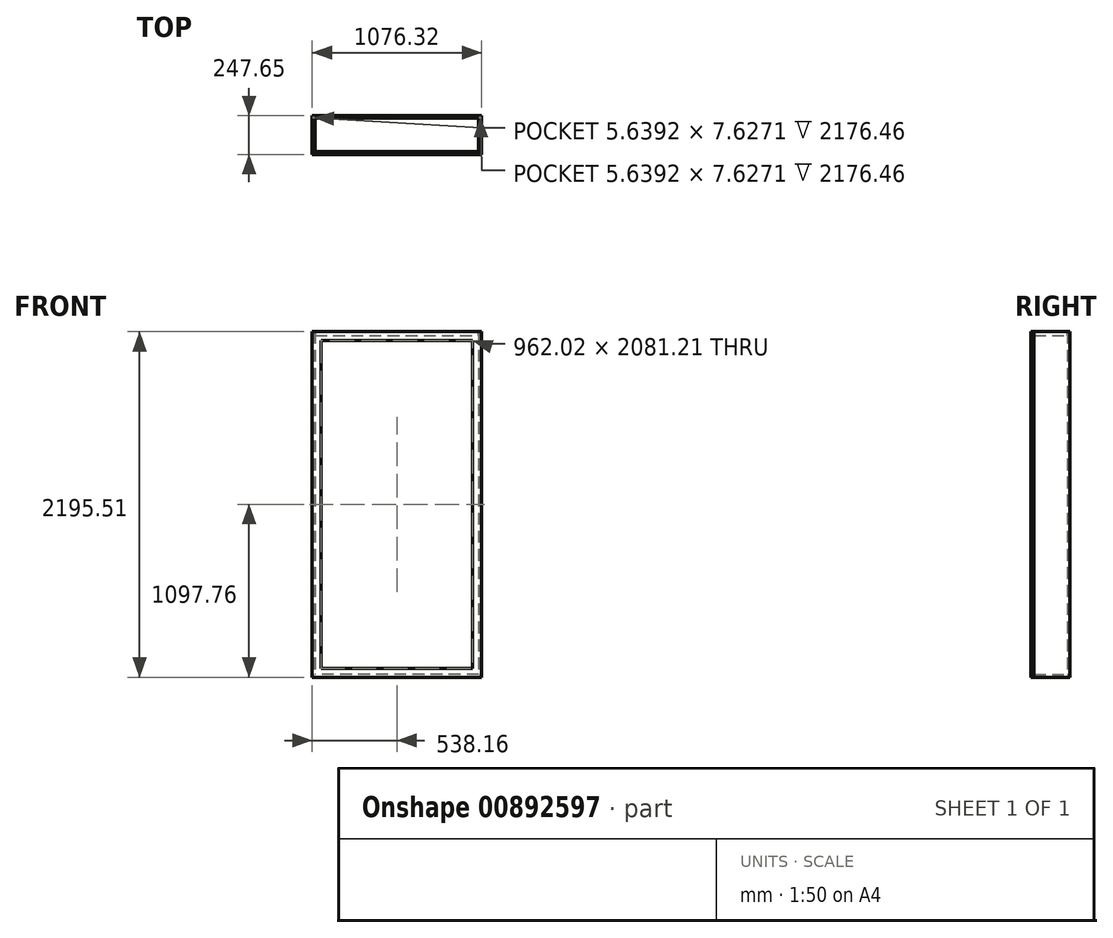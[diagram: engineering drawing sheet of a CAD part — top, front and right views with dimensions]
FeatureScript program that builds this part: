
annotation { "Feature Type Name" : "Feature", "Feature Type Description" : "" }
export const myFeature = defineFeature(function(context is Context, id is Id, definition is map)
    precondition{}
    {
        {
            var Q0;
            Q0=qCreatedBy(makeId("Top.planeOp"),FACE);
            var sketch = newSketch(context, id + "F0", { "sketchPlane" : qUnion([Q0])});
            skLineSegment(sketch, "E0.bottom", {"start": v(538.16, 228.6) * mm, "end": v(-538.16, 228.6) * mm});
            skLineSegment(sketch, "E0.top", {"start": v(538.16, 0) * mm, "end": v(-538.16, 0) * mm});
            skLineSegment(sketch, "E0.left", {"start": v(538.16, 228.6) * mm, "end": v(538.16, 0) * mm});
            skLineSegment(sketch, "E0.right", {"start": v(-538.16, 228.6) * mm, "end": v(-538.16, 0) * mm});
            skSolve(sketch);
        }
        {
            var Q0;
            Q0=makeQuery(id+"F0.imprint","IMPRINT",FACE,{"disambiguationData":[TD([[makeQuery(id+"F0.imprint","IMPRINT",EDGE,{"derivedFrom":sQuery(id+"F0.wireOp",EDGE,"E0.bottom")}),1.0]])]});
            extrude(context, id + "F1", {"entities" : qUnion([Q0]), "depth" : 19.05 * mm, "offsetDistance" : 25.4 * mm});
        }
        {
            var Q0;
            Q0=makeQuery(id+"F1.opExtrude","CAP_FACE",FACE,{"disambiguationData":[OSD([sQuery(id+"F0.wireOp",EDGE,"E0.bottom"),sQuery(id+"F0.wireOp",EDGE,"E0.top"),sQuery(id+"F0.wireOp",EDGE,"E0.left"),sQuery(id+"F0.wireOp",EDGE,"E0.right")])],"isStart":false});
            var sketch = newSketch(context, id + "F2", { "sketchPlane" : qUnion([Q0])});
            skLineSegment(sketch, "E1.bottom", {"start": v(-538.16, 228.6) * mm, "end": v(-519.11, 228.6) * mm});
            skLineSegment(sketch, "E1.top", {"start": v(-538.16, 0) * mm, "end": v(-519.11, 0) * mm});
            skLineSegment(sketch, "E1.left", {"start": v(-538.16, 228.6) * mm, "end": v(-538.16, 0) * mm});
            skLineSegment(sketch, "E1.right", {"start": v(-519.11, 228.6) * mm, "end": v(-519.11, 0) * mm});
            skLineSegment(sketch, "E2.bottom", {"start": v(538.16, 228.6) * mm, "end": v(519.11, 228.6) * mm});
            skLineSegment(sketch, "E2.top", {"start": v(538.16, 0) * mm, "end": v(519.11, 0) * mm});
            skLineSegment(sketch, "E2.left", {"start": v(538.16, 228.6) * mm, "end": v(538.16, 0) * mm});
            skLineSegment(sketch, "E2.right", {"start": v(519.11, 228.6) * mm, "end": v(519.11, 0) * mm});
            skSolve(sketch);
        }
        {
            var Q0;
            Q0=makeQuery(id+"F1.opExtrude","CAP_FACE",FACE,{"disambiguationData":[OSD([sQuery(id+"F0.wireOp",EDGE,"E0.bottom"),sQuery(id+"F0.wireOp",EDGE,"E0.top"),sQuery(id+"F0.wireOp",EDGE,"E0.left"),sQuery(id+"F0.wireOp",EDGE,"E0.right")])],"isStart":false});
            var sketch = newSketch(context, id + "F3", { "sketchPlane" : qUnion([Q0])});
            skLineSegment(sketch, "E3.bottom", {"start": v(-538.16, 0) * mm, "end": v(-519.11, 0) * mm});
            skLineSegment(sketch, "E3.left", {"start": v(-538.16, 0) * mm, "end": v(-538.16, 209.55) * mm});
            skLineSegment(sketch, "E3.right", {"start": v(-519.11, 0) * mm, "end": v(-519.11, 209.55) * mm});
            skLineSegment(sketch, "E4", {"start": v(-528.64, 220.5) * mm, "end": v(-531.46, 220.5) * mm});
            skLineSegment(sketch, "E5", {"start": v(-538.16, 209.55) * mm, "end": v(-538.16, 212.88) * mm});
            skLineSegment(sketch, "E6", {"start": v(-538.16, 212.88) * mm, "end": v(-531.46, 212.88) * mm});
            skLineSegment(sketch, "E7", {"start": v(-531.46, 212.88) * mm, "end": v(-531.46, 220.5) * mm});
            skLineSegment(sketch, "E8.MirrorCS", {"start": v(-528.64, 220.5) * mm, "end": v(-525.82, 220.5) * mm});
            skLineSegment(sketch, "E9.MirrorCS", {"start": v(-525.82, 212.88) * mm, "end": v(-525.82, 220.5) * mm});
            skLineSegment(sketch, "E10.MirrorCS", {"start": v(-519.11, 212.88) * mm, "end": v(-525.82, 212.88) * mm});
            skLineSegment(sketch, "E11.MirrorCS", {"start": v(-519.11, 209.55) * mm, "end": v(-519.11, 212.88) * mm});
            skPoint(sketch, "E12.start.orphan", {"position": v(-528.64, 209.55) * mm});
            skLineSegment(sketch, "E13", {"start": v(0, 0) * mm, "end": v(0, 522.1) * mm});
            skLineSegment(sketch, "E14.MirrorCS", {"start": v(519.11, 0) * mm, "end": v(519.11, 209.55) * mm});
            skLineSegment(sketch, "E15.MirrorCS", {"start": v(519.11, 209.55) * mm, "end": v(519.11, 212.88) * mm});
            skLineSegment(sketch, "E16.MirrorCS", {"start": v(519.11, 212.88) * mm, "end": v(525.82, 212.88) * mm});
            skLineSegment(sketch, "E17.MirrorCS", {"start": v(525.82, 212.88) * mm, "end": v(525.82, 220.5) * mm});
            skLineSegment(sketch, "E18.MirrorCS", {"start": v(528.64, 220.5) * mm, "end": v(525.82, 220.5) * mm});
            skLineSegment(sketch, "E19.MirrorCS", {"start": v(528.64, 220.5) * mm, "end": v(531.46, 220.5) * mm});
            skLineSegment(sketch, "E20.MirrorCS", {"start": v(531.46, 212.88) * mm, "end": v(531.46, 220.5) * mm});
            skLineSegment(sketch, "E21.MirrorCS", {"start": v(538.16, 212.88) * mm, "end": v(531.46, 212.88) * mm});
            skLineSegment(sketch, "E22.bottom", {"start": v(-538.16, 228.6) * mm, "end": v(538.16, 228.6) * mm});
            skLineSegment(sketch, "E22.top", {"start": v(-538.16, 212.88) * mm, "end": v(538.16, 212.88) * mm});
            skLineSegment(sketch, "E22.left", {"start": v(-538.16, 228.6) * mm, "end": v(-538.16, 212.88) * mm});
            skLineSegment(sketch, "E22.right", {"start": v(538.16, 228.6) * mm, "end": v(538.16, 212.88) * mm});
            skSolve(sketch);
        }
        {
            var Q0;
            {var subQ0=sQuery(id+"F3.wireOp",EDGE,"E17.MirrorCS");Q0=makeQuery(id+"F3.imprint","IMPRINT",FACE,{"disambiguationData":[TD([[makeQuery(id+"F3.imprint","IMPRINT",EDGE,{"derivedFrom":subQ0}),1.0]])]});}
            var Q1;
            Q1=makeQuery(id+"F3.imprint","IMPRINT",FACE,{"disambiguationData":[TD([[makeQuery(id+"F3.imprint","IMPRINT",EDGE,{"derivedFrom":sQuery(id+"F3.wireOp",EDGE,"E4")}),-1.0]])]});
            var Q2;
            Q2=makeQuery(id+"F3.imprint","IMPRINT",FACE,{"disambiguationData":[TD([[makeQuery(id+"F3.imprint","IMPRINT",EDGE,{"derivedFrom":sQuery(id+"F3.wireOp",EDGE,"E3.bottom")}),-1.0]])]});
            var Q3;
            {var subQ4=sQuery(id+"F3.wireOp",EDGE,"E14.MirrorCS");Q3=makeQuery(id+"F3.imprint","IMPRINT",FACE,{"disambiguationData":[TD([[makeQuery(id+"F3.imprint","IMPRINT",EDGE,{"derivedFrom":subQ4}),-1.0]])]});}
            extrude(context, id + "F4", {"entities" : qUnion([Q0, Q1, Q2, Q3]), "operationType" : NewBodyOperationType.ADD, "depth" : 2176.46 * mm, "offsetDistance" : 25.4 * mm});
        }
        {
            var Q0;
            Q0=makeQuery(id+"F4.opExtrude","CAP_FACE",FACE,{"disambiguationData":[OSD([sQuery(id+"F0.wireOp",EDGE,"E0.top"),sQuery(id+"F0.wireOp",EDGE,"E0.left"),sQuery(id+"F3.wireOp",EDGE,"E3.bottom"),sQuery(id+"F3.wireOp",EDGE,"E3.left"),sQuery(id+"F3.wireOp",EDGE,"E3.right"),sQuery(id+"F3.wireOp",EDGE,"E4"),sQuery(id+"F3.wireOp",EDGE,"E5"),sQuery(id+"F3.wireOp",EDGE,"E7"),sQuery(id+"F3.wireOp",EDGE,"E8.MirrorCS"),sQuery(id+"F3.wireOp",EDGE,"E9.MirrorCS"),sQuery(id+"F3.wireOp",EDGE,"E11.MirrorCS"),sQuery(id+"F3.wireOp",EDGE,"E14.MirrorCS"),sQuery(id+"F3.wireOp",EDGE,"E15.MirrorCS"),sQuery(id+"F3.wireOp",EDGE,"E17.MirrorCS"),sQuery(id+"F3.wireOp",EDGE,"E18.MirrorCS"),sQuery(id+"F3.wireOp",EDGE,"E19.MirrorCS"),sQuery(id+"F3.wireOp",EDGE,"E20.MirrorCS"),sQuery(id+"F3.wireOp",EDGE,"E22.bottom"),sQuery(id+"F3.wireOp",EDGE,"E22.top"),sQuery(id+"F3.wireOp",EDGE,"E22.left"),sQuery(id+"F3.wireOp",EDGE,"E22.right")])],"isStart":false});
            var sketch = newSketch(context, id + "F5", { "sketchPlane" : qUnion([Q0])});
            skLineSegment(sketch, "E23.bottom", {"start": v(-519.11, 0) * mm, "end": v(519.11, 0) * mm});
            skLineSegment(sketch, "E23.top", {"start": v(-519.11, 212.88) * mm, "end": v(519.11, 212.88) * mm});
            skLineSegment(sketch, "E23.left", {"start": v(-519.11, 0) * mm, "end": v(-519.11, 212.88) * mm});
            skLineSegment(sketch, "E23.right", {"start": v(519.11, 0) * mm, "end": v(519.11, 212.88) * mm});
            skSolve(sketch);
        }
        {
            var Q0;
            Q0 = qSketchRegion(id + "F5", true);
            extrude(context, id + "F6", {"entities" : qUnion([Q0]), "oppositeDirection" : true, "depth" : 25.4 * mm, "offsetDistance" : 25.4 * mm});
        }
        {
            var Q0;
            {var subQ0=sQuery(id+"F0.wireOp",EDGE,"E0.top");Q0=makeQuery(id+"F4.boolean.opBoolean","MERGE",FACE,{"derivedFrom":[makeQuery(id+"F1.opExtrude","SWEPT_FACE",FACE,{"disambiguationData":[OSD([subQ0])]}),makeQuery(id+"F4.opExtrude","SWEPT_FACE",FACE,{"disambiguationData":[OSD([sQuery(id+"F3.wireOp",EDGE,"E3.bottom")])]}),makeQuery(id+"F4.opExtrude","SWEPT_FACE",FACE,{"disambiguationData":[OSD([subQ0])]})]});}
            var sketch = newSketch(context, id + "F7", { "sketchPlane" : qUnion([Q0])});
            skLineSegment(sketch, "E24.bottom", {"start": v(538.16, 0) * mm, "end": v(-538.16, 0) * mm});
            skLineSegment(sketch, "E24.top", {"start": v(538.16, 2195.51) * mm, "end": v(-538.16, 2195.51) * mm});
            skLineSegment(sketch, "E24.left", {"start": v(538.16, 0) * mm, "end": v(538.16, 2195.51) * mm});
            skLineSegment(sketch, "E24.right", {"start": v(-538.16, 0) * mm, "end": v(-538.16, 2195.51) * mm});
            skLineSegment(sketch, "E25.0", {"start": v(-481.01, 57.15) * mm, "end": v(-481.01, 2138.36) * mm});
            skLineSegment(sketch, "E25.1", {"start": v(481.01, 57.15) * mm, "end": v(-481.01, 57.15) * mm});
            skLineSegment(sketch, "E25.2", {"start": v(481.01, 57.15) * mm, "end": v(481.01, 2138.36) * mm});
            skLineSegment(sketch, "E25.3", {"start": v(481.01, 2138.36) * mm, "end": v(-481.01, 2138.36) * mm});
            skSolve(sketch);
        }
        {
            var Q0;
            Q0 = qSketchRegion(id + "F7", true);
            extrude(context, id + "F8", {"entities" : qUnion([Q0]), "depth" : 19.05 * mm, "offsetDistance" : 25.4 * mm});
        }
    });
